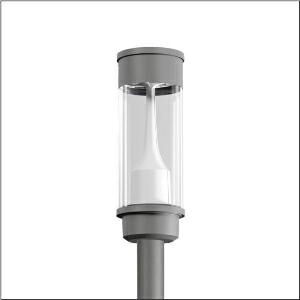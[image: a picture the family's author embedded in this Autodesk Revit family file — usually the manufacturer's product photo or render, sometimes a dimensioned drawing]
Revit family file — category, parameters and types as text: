
# Revit family: litepole_iq___pl1_2s_5xa5415of14h_b306
name_source: partatom
category: Lighting Fixtures
units: mm (PartAtom-declared; Revit-internal decimal feet)

## family parameters
Cut with Voids When Loaded = No
Host = Face
Light Source = No
Part Type = Normal
Room Calculation Point = No
Round Connector Dimension = Use Diameter
Shared = No

## types (1)
- --- (1 x LED, 2970 lm, 21.8 W, 2700K)
    Apparent Load = 22 VA
    CIE Flux Codes = 23 62 94 96 100
    Color Rendering = 70
    Color Temperature = 2700K
    Default Elevation = 1800 mm
    Description = Litepole iQ, mast luminaire, Module 540 iQ-SR, primary light control with 3 zone facetted reflector, of plastic, silver coated, highly specular, structured, primary optical cover: cover, of PMMA, transparent, partly coated, light distribution: PL1.2s, light emission: direct distribution, primary light characteristic: symmetric, installation type: post-top, LED, High Power LED, rated luminous flux: 2.970lm, luminous efficacy: 136lm/W, light colour: 727, colour temperature: 2700K, control gear: ECG iQ, control: optimised constant luminous flux control (CLO 2.0), Desk-Remote (wireless, voltage-free reading and setting of iQ features in the workshop via application-optimized NFC function/RFID function), Light-Fading, Smart-Wire, Night-Set, Lumen-Switch, Temp-Guard, Auto-Match, Street-Remote, pre-setting: logarithmic dimming characteristic, with terminal, 6-pole, max. 2.5mm², mains connection: 230..240V, AC, 50/60Hz, start of lifetime: 22W, end of service life: 23W, reduction: 11W, luminaire housing, upper part, of glass-fibre reinforced polyester, coated, Siteco® metallic grey (DB 702S), diameter: 210mm, height: 590mm, spigot size: d x l = 76 x 70mm (post-top) | with reducer (optional accessory) 60 x 70mm, post-top mast mounting element, of diecast aluminium, coated, Siteco® metallic grey (DB 702S), Module 540 iQ-SR, traffic white (RAL 9016), equipment: standard, protection rating (complete): IP65, insulation class (complete): insulation class II (safety insulation), certification: CE, ENEC, VDE, packaging unit: 1 piece

Light Distribution: PL1.2s
    Height = 590 mm
    Lamp = 1 x LED
    Lamp Light Flux = 2970 lm
    Lamp Power = 21.8 W
    Lamp count = 1
    Length = 220 mm
    Luminous efficacy = 136 lm/W
    Manufacturer = Siteco
    ModVariant = No
    Model = 5XA5415OF14H
    Number of Poles = 1
    OnlyDefault = Yes
    Power Factor = 1
    Product Name = Litepole iQ | PL1.2s
    Product group = mast luminaire | pylon top
    ProductGroupID = 6100
    Protection Class = Protection class II
    Protection Degree = IP 65
    RLX_Detail_Level = 1
    RLX_Emergency_Light_Flux = 0 lm
    RLX_Emergency_Type = 0
    RLX_Emergency_Type_DB = No
    RlxData = <blob elided: 39833 chars, md5=a7300e83>
    Socket = socket
    Standby Power = 0 W
    System Light Flux = 2970 lm
    System Power = 22 W
    Type Comments = factory setting: luminous flux: 100 % | dim-lin: 254 | 456 mA
    Type Image = l_1006025.jpg
    URL = http://relux.com
    VarID = @adj_114649
    Voltage = 0 V
    Weight = 0.00 kg
    Width = 0 mm  [stored 0 ft]

note: [stored X ft] marks values corroborated as IEEE doubles in the binary element streams (Revit-internal decimal feet)

## geometry (parser evidence)
native form markers: Blend x4, Sweep x10
no freeform markers — native parametric forms only
